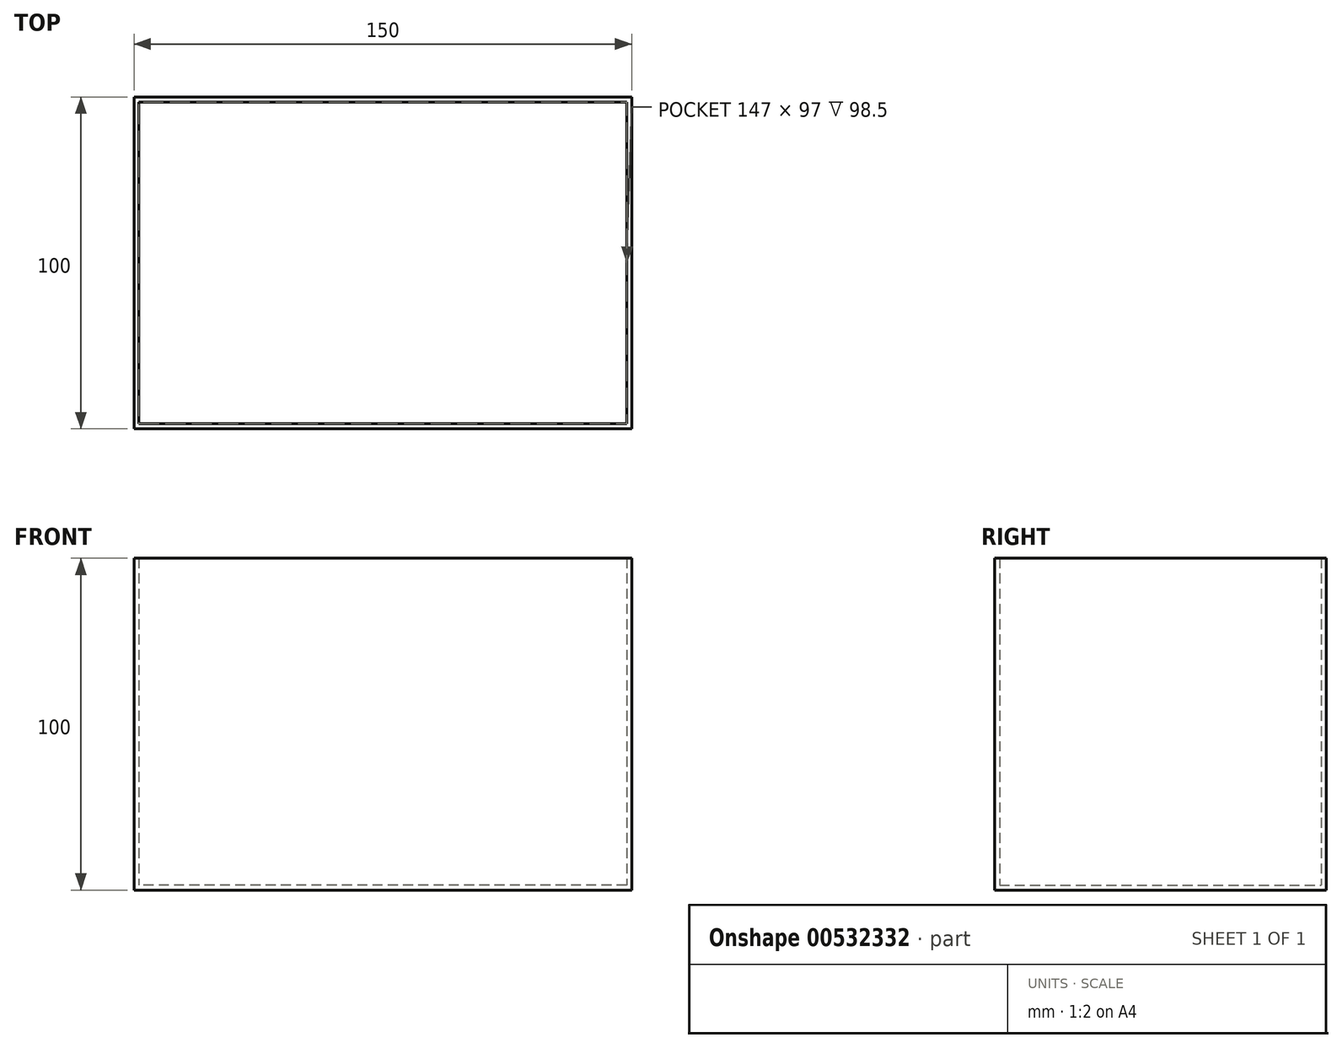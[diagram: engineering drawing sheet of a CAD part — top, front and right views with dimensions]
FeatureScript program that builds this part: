
annotation { "Feature Type Name" : "Feature", "Feature Type Description" : "" }
export const myFeature = defineFeature(function(context is Context, id is Id, definition is map)
    precondition{}
    {
        {
            var Q0;
            Q0=qCreatedBy(makeId("Front.planeOp"),FACE);
            var sketch = newSketch(context, id + "F0", { "sketchPlane" : qUnion([Q0])});
            skLineSegment(sketch, "E0.bottom", {"start": v(75, 50) * mm, "end": v(-75, 50) * mm});
            skLineSegment(sketch, "E0.top", {"start": v(75, -50) * mm, "end": v(-75, -50) * mm});
            skLineSegment(sketch, "E0.left", {"start": v(75, 50) * mm, "end": v(75, -50) * mm});
            skLineSegment(sketch, "E0.right", {"start": v(-75, 50) * mm, "end": v(-75, -50) * mm});
            skPoint(sketch, "E0.middle", {"position": v(0, 0) * mm});
            skSolve(sketch);
        }
        {
            var Q0;
            Q0 = qSketchRegion(id + "F0", true);
            extrude(context, id + "F1", {"entities" : qUnion([Q0]), "endBound" : BoundingType.SYMMETRIC, "depth" : 100 * mm, "offsetDistance" : 25 * mm});
        }
        {
            var Q0;
            Q0=makeQuery(id+"F1.opExtrude","SWEPT_FACE",FACE,{"disambiguationData":[OSD([sQuery(id+"F0.wireOp",EDGE,"E0.bottom")])]});
            shell(context, id + "F2", {"entities" : qUnion([Q0]), "thickness" : 1.5 * mm});
        }
    });
